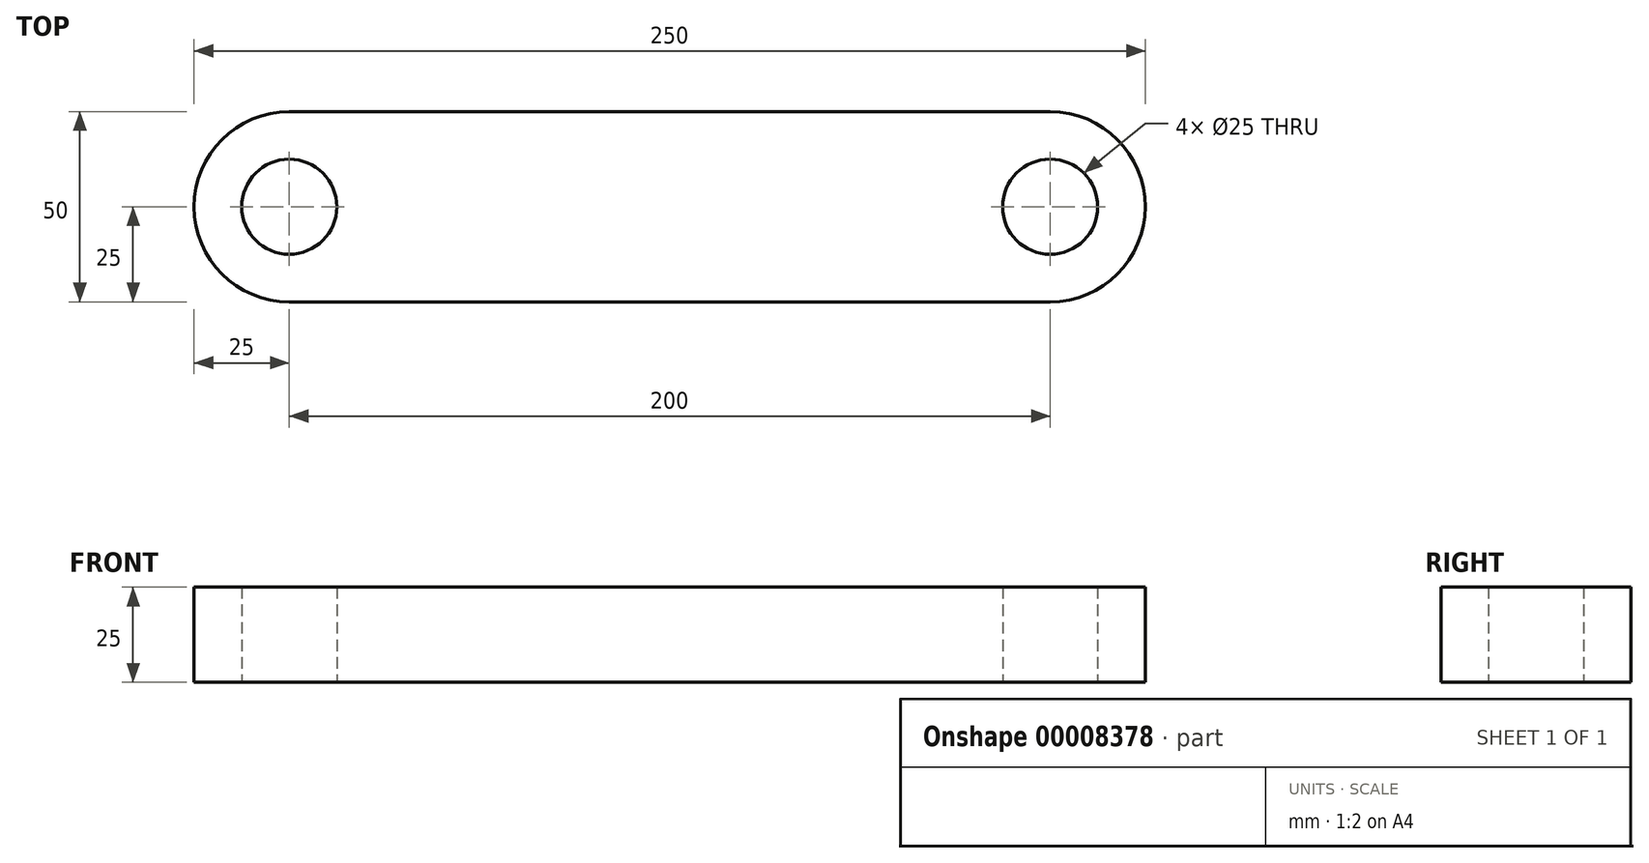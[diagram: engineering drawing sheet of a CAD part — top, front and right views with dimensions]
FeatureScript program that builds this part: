
annotation { "Feature Type Name" : "Feature", "Feature Type Description" : "" }
export const myFeature = defineFeature(function(context is Context, id is Id, definition is map)
    precondition{}
    {
        {
            var Q0;
            Q0=qCreatedBy(makeId("Top.planeOp"),FACE);
            var sketch = newSketch(context, id + "F0", { "sketchPlane" : qUnion([Q0])});
            skLineSegment(sketch, "E0.rect.bottom", {"start": v(100, 25) * mm, "end": v(-100, 25) * mm});
            skLineSegment(sketch, "E0.rect.top", {"start": v(100, -25) * mm, "end": v(-100, -25) * mm});
            skPoint(sketch, "E0.rect.middle", {"position": v(0, 0) * mm});
            skArc(sketch, "E1", {"start": v(-100, 25) * mm, "mid": v(-125, 0) * mm, "end": v(-100, -25) * mm});
            skArc(sketch, "E2", {"start": v(100, -25) * mm, "mid": v(125, 0) * mm, "end": v(100, 25) * mm});
            skCircle(sketch, "E3", {"center": v(100, 0) * mm, "radius": 12.5 * mm});
            skCircle(sketch, "E4", {"center": v(-100, 0) * mm, "radius": 12.5 * mm});
            skSolve(sketch);
        }
        {
            var Q0;
            Q0 = qSketchRegion(id + "F0", true);
            extrude(context, id + "F1", {"entities" : qUnion([Q0]), "depth" : 25 * mm});
        }
    });
